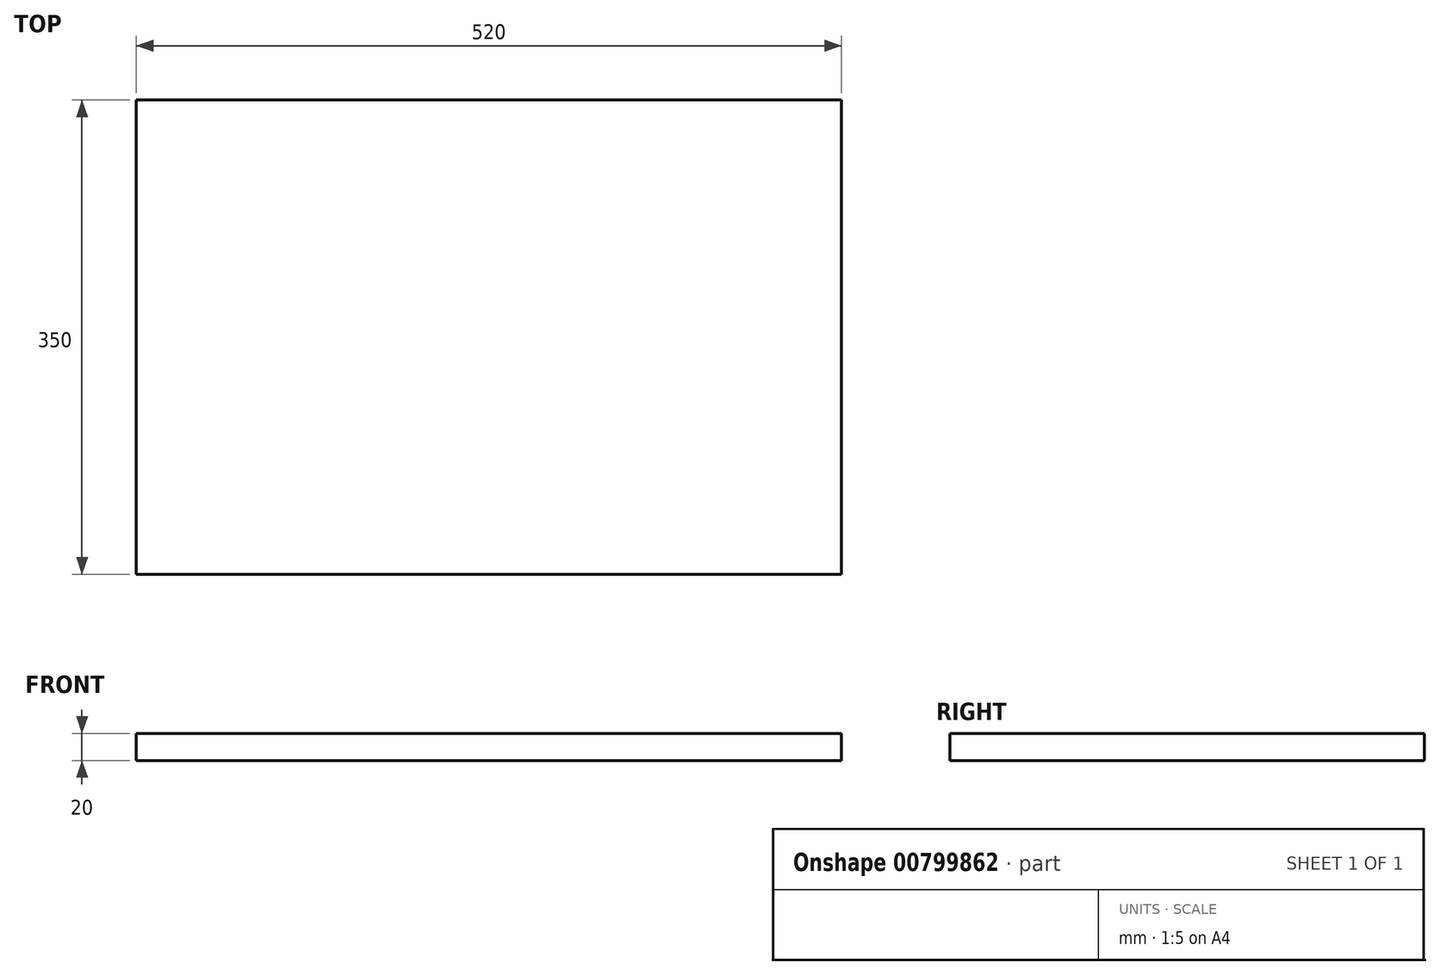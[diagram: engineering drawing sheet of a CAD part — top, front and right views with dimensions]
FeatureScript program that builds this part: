
annotation { "Feature Type Name" : "Feature", "Feature Type Description" : "" }
export const myFeature = defineFeature(function(context is Context, id is Id, definition is map)
    precondition{}
    {
        {
            var Q0;
            Q0=qCreatedBy(makeId("Top.planeOp"),FACE);
            var sketch = newSketch(context, id + "F0", { "sketchPlane" : qUnion([Q0])});
            skLineSegment(sketch, "E0.bottom", {"start": v(260, -175) * mm, "end": v(-260, -175) * mm});
            skLineSegment(sketch, "E0.top", {"start": v(260, 175) * mm, "end": v(-260, 175) * mm});
            skLineSegment(sketch, "E0.left", {"start": v(260, -175) * mm, "end": v(260, 175) * mm});
            skLineSegment(sketch, "E0.right", {"start": v(-260, -175) * mm, "end": v(-260, 175) * mm});
            skPoint(sketch, "E0.middle", {"position": v(0, 0) * mm});
            skSolve(sketch);
        }
        {
            var Q0;
            Q0=makeQuery(id+"F0.imprint","IMPRINT",FACE,{"disambiguationData":[TD([[makeQuery(id+"F0.imprint","IMPRINT",EDGE,{"derivedFrom":sQuery(id+"F0.wireOp",EDGE,"E0.bottom")}),-1.0]])]});
            extrude(context, id + "F1", {"entities" : qUnion([Q0]), "depth" : 20 * mm, "offsetDistance" : 25 * mm});
        }
    });
